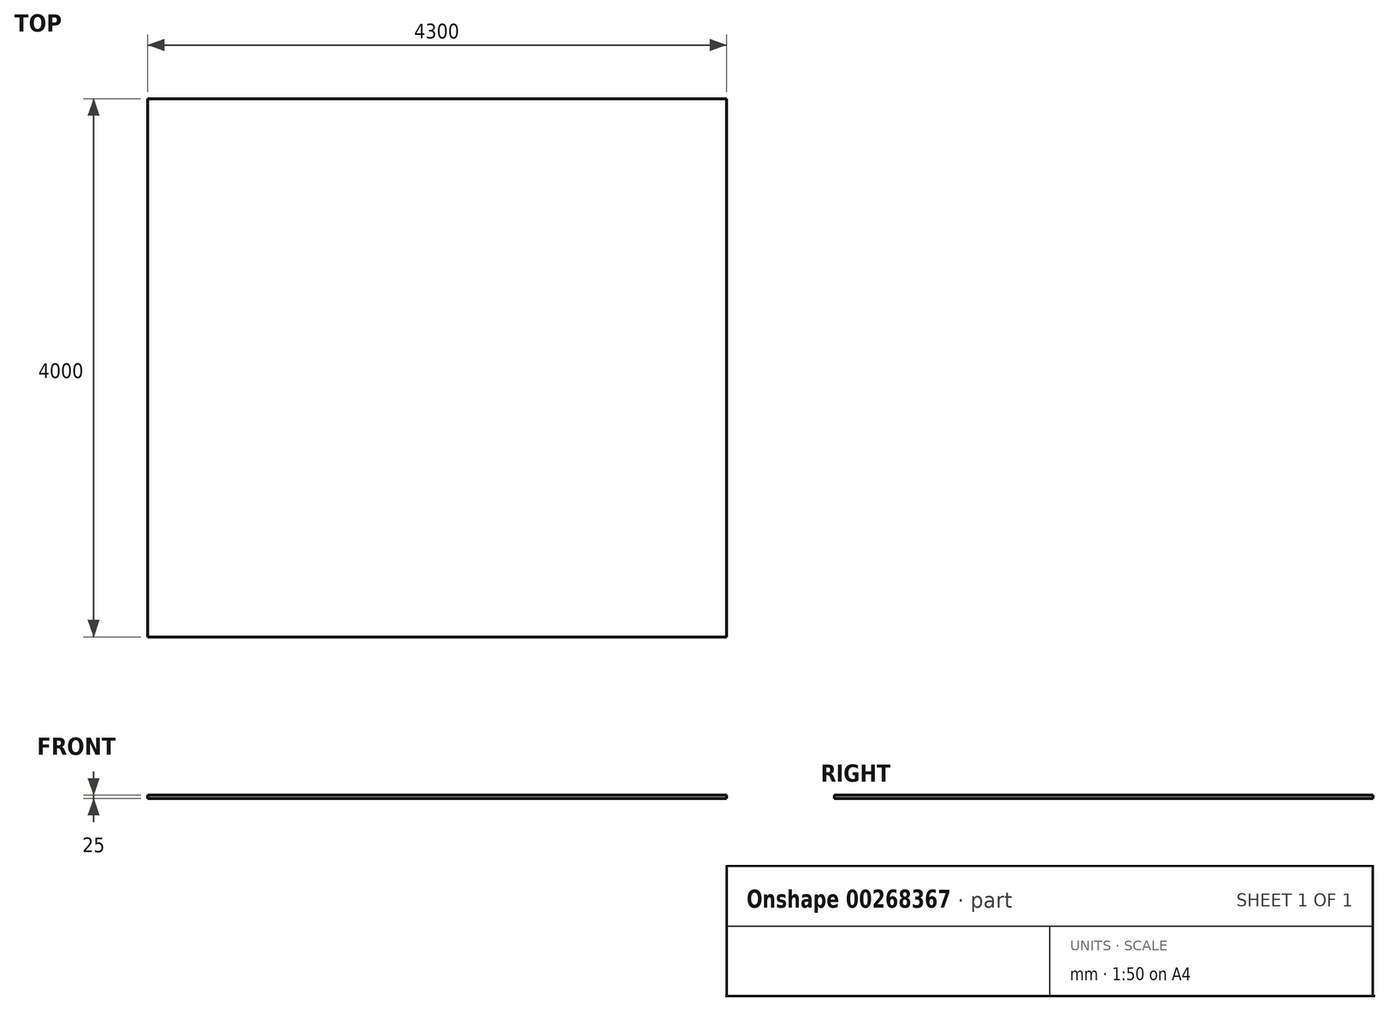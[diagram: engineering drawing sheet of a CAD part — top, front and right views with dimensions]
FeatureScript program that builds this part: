
annotation { "Feature Type Name" : "Feature", "Feature Type Description" : "" }
export const myFeature = defineFeature(function(context is Context, id is Id, definition is map)
    precondition{}
    {
        {
            var Q0;
            Q0=qCreatedBy(makeId("Top.planeOp"),FACE);
            var sketch = newSketch(context, id + "F0", { "sketchPlane" : qUnion([Q0])});
            skLineSegment(sketch, "E0.bottom", {"start": v(-4230.85, 3936.58) * mm, "end": v(69.15, 3936.58) * mm});
            skLineSegment(sketch, "E0.top", {"start": v(-4230.85, -63.42) * mm, "end": v(69.15, -63.42) * mm});
            skLineSegment(sketch, "E0.left", {"start": v(-4230.85, 3936.58) * mm, "end": v(-4230.85, -63.42) * mm});
            skLineSegment(sketch, "E0.right", {"start": v(69.15, 3936.58) * mm, "end": v(69.15, -63.42) * mm});
            skSolve(sketch);
        }
        {
            var Q0;
            Q0=makeQuery(id+"F0.imprint","IMPRINT",FACE,{"disambiguationData":[TD([[makeQuery(id+"F0.imprint","IMPRINT",EDGE,{"derivedFrom":sQuery(id+"F0.wireOp",EDGE,"E0.bottom")}),-1.0]])]});
            extrude(context, id + "F1", {"entities" : qUnion([Q0]), "depth" : 25 * mm});
        }
    });
